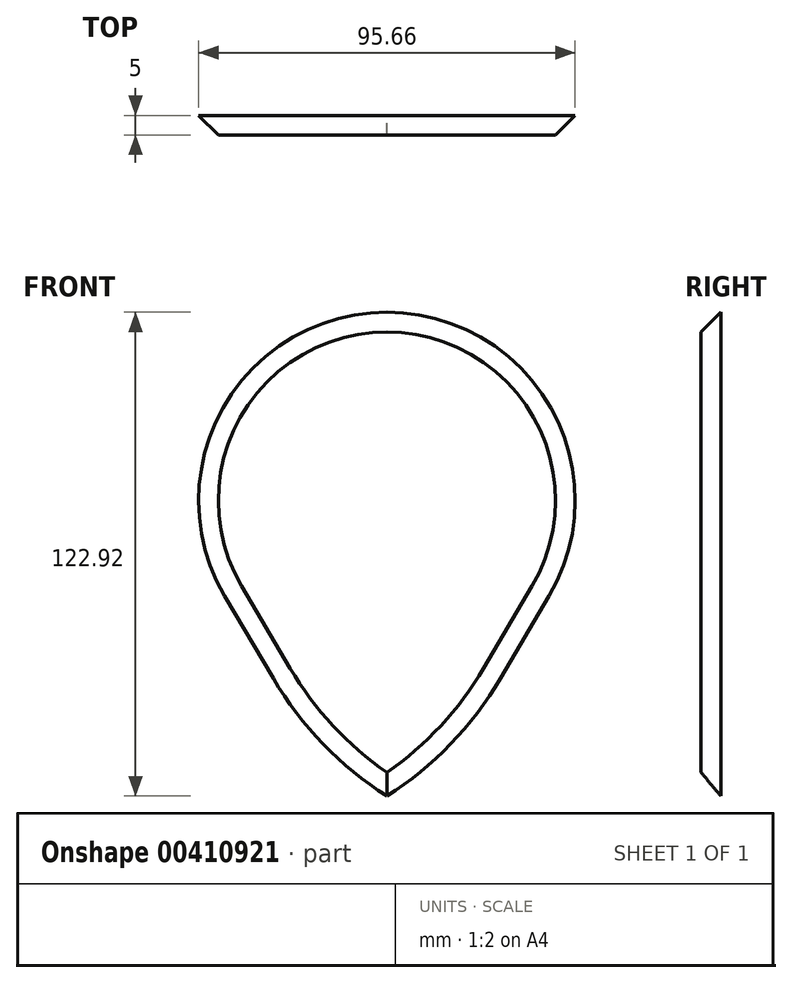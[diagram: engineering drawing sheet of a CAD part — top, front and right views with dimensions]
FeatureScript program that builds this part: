
annotation { "Feature Type Name" : "Feature", "Feature Type Description" : "" }
export const myFeature = defineFeature(function(context is Context, id is Id, definition is map)
    precondition{}
    {
        {
            var Q0;
            Q0=qCreatedBy(makeId("Front.planeOp"),FACE);
            var sketch = newSketch(context, id + "F0", { "sketchPlane" : qUnion([Q0])});
            skCircle(sketch, "E0", {"center": v(0, 0) * mm, "radius": 47.83 * mm});
            skLineSegment(sketch, "E1", {"start": v(-28.86, -45.22) * mm, "end": v(-41.2, -24.3) * mm});
            skArc(sketch, "E2", {"start": v(-28.86, -45.22) * mm, "mid": v(-16.2, -61.86) * mm, "end": v(0, -75.09) * mm});
            skLineSegment(sketch, "E3.MirrorCS", {"start": v(28.86, -45.22) * mm, "end": v(41.2, -24.3) * mm});
            skArc(sketch, "E4.MirrorCS", {"start": v(28.86, -45.22) * mm, "mid": v(16.2, -61.86) * mm, "end": v(0, -75.09) * mm});
            skSolve(sketch);
        }
        {
            var Q0;
            Q0 = qSketchRegion(id + "F0", true);
            extrude(context, id + "F1", {"entities" : qUnion([Q0]), "depth" : 5 * mm, "hasDraft" : true, "draftAngle" : 45 * degree, "draftPullDirection" : true});
        }
    });
